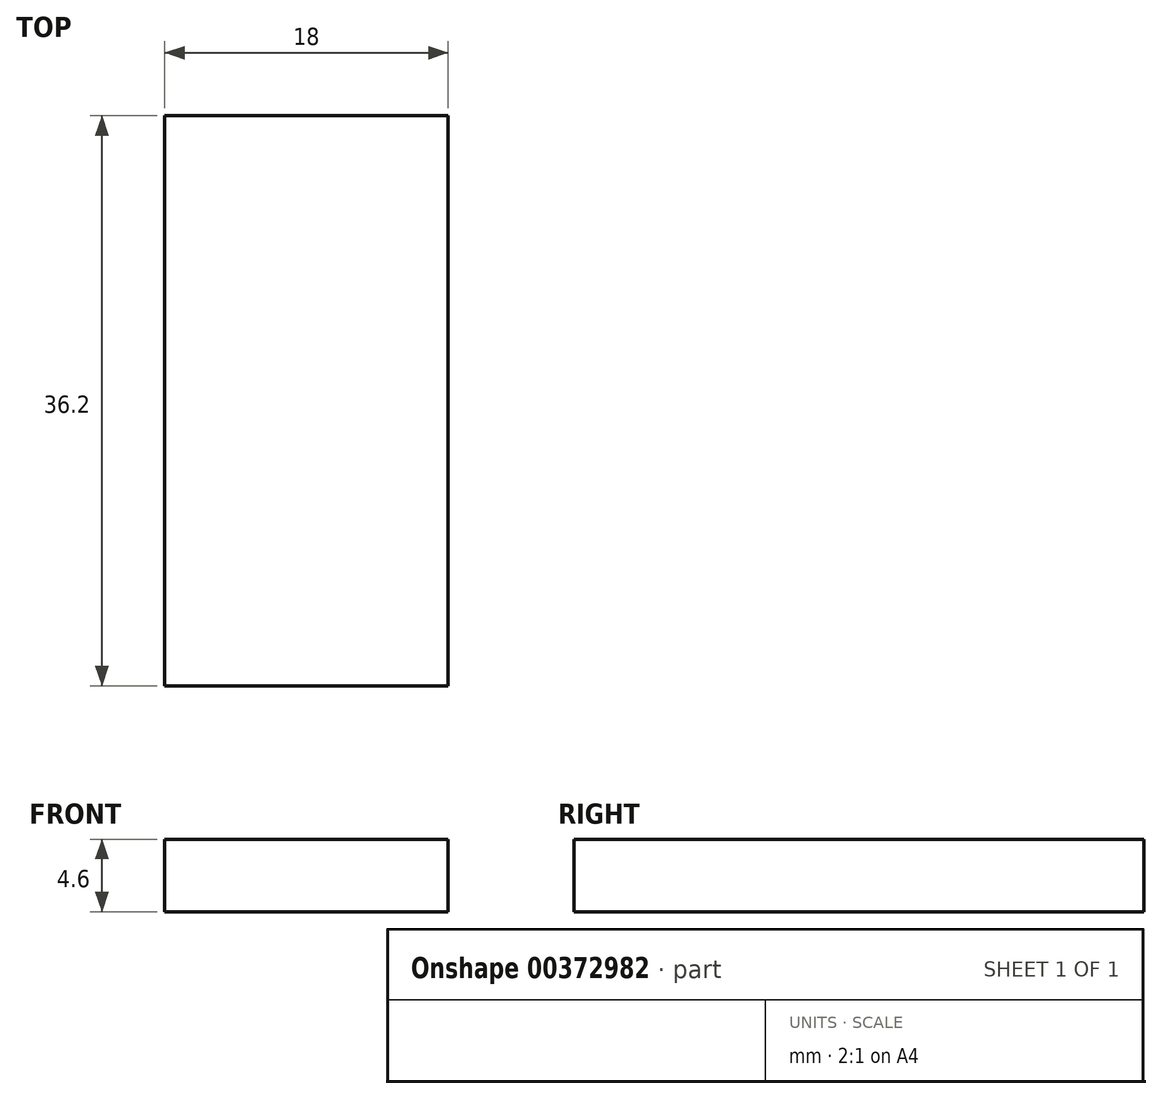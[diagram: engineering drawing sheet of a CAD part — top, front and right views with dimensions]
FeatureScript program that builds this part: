
annotation { "Feature Type Name" : "Feature", "Feature Type Description" : "" }
export const myFeature = defineFeature(function(context is Context, id is Id, definition is map)
    precondition{}
    {
        {
            var Q0;
            Q0=qCreatedBy(makeId("Top.planeOp"),FACE);
            var sketch = newSketch(context, id + "F0", { "sketchPlane" : qUnion([Q0])});
            skLineSegment(sketch, "E0.bottom", {"start": v(-9, -18.1) * mm, "end": v(9, -18.1) * mm});
            skLineSegment(sketch, "E0.top", {"start": v(-9, 18.1) * mm, "end": v(9, 18.1) * mm});
            skLineSegment(sketch, "E0.left", {"start": v(-9, -18.1) * mm, "end": v(-9, 18.1) * mm});
            skLineSegment(sketch, "E0.right", {"start": v(9, -18.1) * mm, "end": v(9, 18.1) * mm});
            skPoint(sketch, "E0.middle", {"position": v(0, 0) * mm});
            skSolve(sketch);
        }
        {
            var Q0;
            Q0 = qSketchRegion(id + "F0", true);
            extrude(context, id + "F1", {"entities" : qUnion([Q0]), "depth" : 4.6 * mm, "offsetDistance" : 25 * mm});
        }
    });
